# Revit family: CL 55 2 feed-heads 2 speeds (a)
name_source: partatom
category: Equipement spécialisé
revit_build: Autodesk Revit LT 2015 (Build: 20140606_1530(x64)
units: mm (PartAtom-declared; Revit-internal decimal feet)

## types (3) — shared parameters
Apparent Power = 0 VA
Depth Goulotte Auto = 385 mm  [stored 1.26312 ft]
Depth Goulotte à Levier = 365 mm  [stored 1.19751 ft]
Description = COUPE-LEGUMES
Electrique connexion Goulotte Auto = 292 mm  [stored 0.958005 ft]
Electrique connexion Goulotte à levier = 152 mm  [stored 0.498688 ft]
Fabricant = ROBOT COUPE
Height Goulotte Auto = 1298 mm  [stored 4.25853 ft]
Height Goulotte à Levier = 1135 mm  [stored 3.72375 ft]
Modèle = CL55 2 feed-heads 2 speeds
Phase = 3
Speeds (Rpm) = 375 & 750
UP Depth Goulotte Auto = 821 mm  [stored 2.69357 ft]
UP Depth Goulotte à Levier = 645 mm  [stored 2.11614 ft]
UP Height Goulotte à Levier = 1320 mm
URL = www.robot-coupe.com
Weight = 51.3 Kg
Width Goulotte à Levier = 720 mm  [stored 2.3622 ft]
water = Connector
zero-valued in all types: Cold water supply, Cold water supply height, Used water, Waste water height

## per-type parameters (varying)
| type | Amps | Cycle | Volts |
| CL55 2 feed-heads 2 speeds   400/50/3 | 2,7 A | 50 Hz | 400 V |
| CL55 2 feed-heads 2 speeds   220/60/3 | 5,3 A | 60 Hz | 220 V |
| CL55 2 feed-heads 2 speeds   380/60/3 | 2,7 A | 60 Hz | 380 V |

note: [stored X ft] marks values corroborated as IEEE doubles in the binary element streams (Revit-internal decimal feet)

## geometry (parser evidence)
native form markers: Blend x94, Sweep x5
no freeform markers — native parametric forms only
